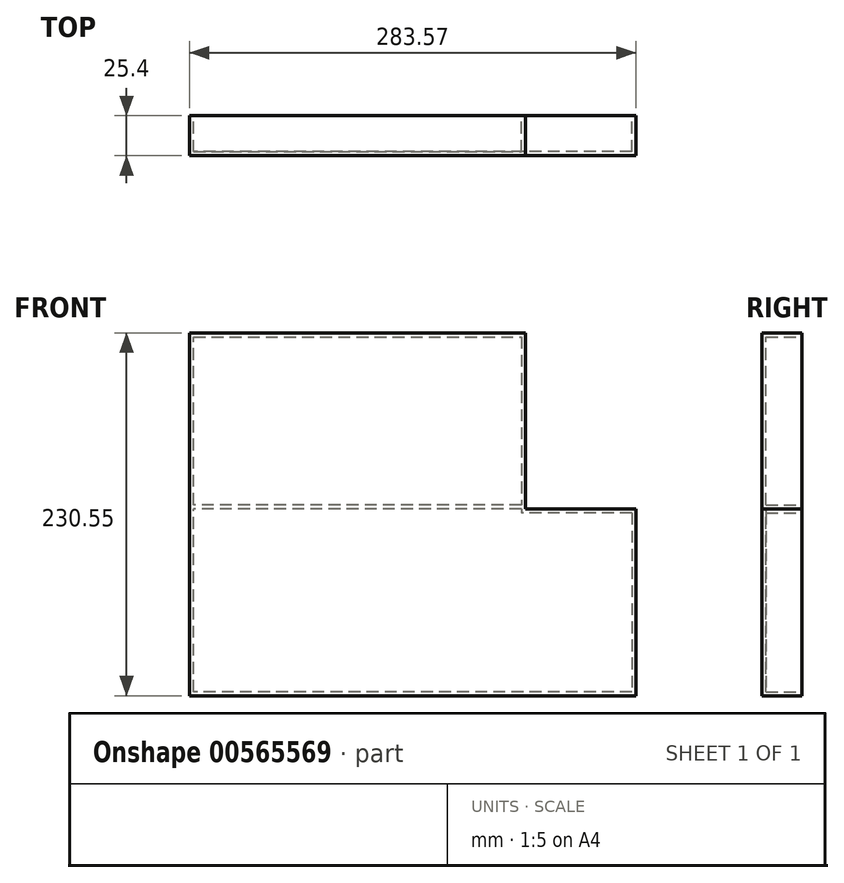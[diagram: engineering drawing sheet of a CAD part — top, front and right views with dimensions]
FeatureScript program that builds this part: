
annotation { "Feature Type Name" : "Feature", "Feature Type Description" : "" }
export const myFeature = defineFeature(function(context is Context, id is Id, definition is map)
    precondition{}
    {
        {
            var Q0;
            Q0=qCreatedBy(makeId("Front.planeOp"),FACE);
            var sketch = newSketch(context, id + "F0", { "sketchPlane" : qUnion([Q0])});
            skLineSegment(sketch, "E0", {"start": v(0, 111.76) * mm, "end": v(213.36, 111.76) * mm});
            skLineSegment(sketch, "E1", {"start": v(213.36, 111.76) * mm, "end": v(213.36, 0) * mm});
            skLineSegment(sketch, "E2", {"start": v(213.36, 0) * mm, "end": v(0, 0) * mm});
            skLineSegment(sketch, "E3", {"start": v(0, 0) * mm, "end": v(0, 111.76) * mm});
            skSolve(sketch);
        }
        {
            var Q0;
            Q0 = qSketchRegion(id + "F0", true);
            extrude(context, id + "F1", {"entities" : qUnion([Q0]), "depth" : 25.4 * mm, "offsetDistance" : 25.4 * mm});
        }
        {
            var Q0;
            Q0=makeQuery(id+"F1.opExtrude","CAP_FACE",FACE,{"disambiguationData":[OSD([sQuery(id+"F0.wireOp",EDGE,"E0"),sQuery(id+"F0.wireOp",EDGE,"E1"),sQuery(id+"F0.wireOp",EDGE,"E2"),sQuery(id+"F0.wireOp",EDGE,"E3")])],"isStart":true});
            shell(context, id + "F2", {"entities" : qUnion([Q0]), "thickness" : 2.54 * mm});
        }
        {
            var Q0;
            Q0=qCreatedBy(makeId("Front.planeOp"),FACE);
            var sketch = newSketch(context, id + "F3", { "sketchPlane" : qUnion([Q0])});
            skLineSegment(sketch, "E4.bottom", {"start": v(283.57, 0) * mm, "end": v(0, 0) * mm});
            skLineSegment(sketch, "E4.top", {"start": v(283.57, -118.8) * mm, "end": v(0, -118.8) * mm});
            skLineSegment(sketch, "E4.left", {"start": v(283.57, 0) * mm, "end": v(283.57, -118.8) * mm});
            skLineSegment(sketch, "E4.right", {"start": v(0, 0) * mm, "end": v(0, -118.8) * mm});
            skSolve(sketch);
        }
        {
            var Q0;
            Q0 = qSketchRegion(id + "F3", true);
            extrude(context, id + "F4", {"entities" : qUnion([Q0]), "operationType" : NewBodyOperationType.ADD, "depth" : 25.4 * mm, "offsetDistance" : 25.4 * mm});
        }
        {
            var Q0;
            Q0=makeQuery(id+"F4.boolean.opBoolean","MERGE",FACE,{"derivedFrom":[makeQuery(id+"F1.opExtrude","CAP_FACE",FACE,{"disambiguationData":[OSD([sQuery(id+"F0.wireOp",EDGE,"E0"),sQuery(id+"F0.wireOp",EDGE,"E1"),sQuery(id+"F0.wireOp",EDGE,"E2"),sQuery(id+"F0.wireOp",EDGE,"E3")])],"isStart":true}),makeQuery(id+"F4.opExtrude","CAP_FACE",FACE,{"disambiguationData":[OSD([sQuery(id+"F3.wireOp",EDGE,"E4.bottom"),sQuery(id+"F3.wireOp",EDGE,"E4.top"),sQuery(id+"F3.wireOp",EDGE,"E4.left"),sQuery(id+"F3.wireOp",EDGE,"E4.right")])],"isStart":true})]});
            shell(context, id + "F5", {"entities" : qUnion([Q0]), "thickness" : 2.54 * mm});
        }
    });
